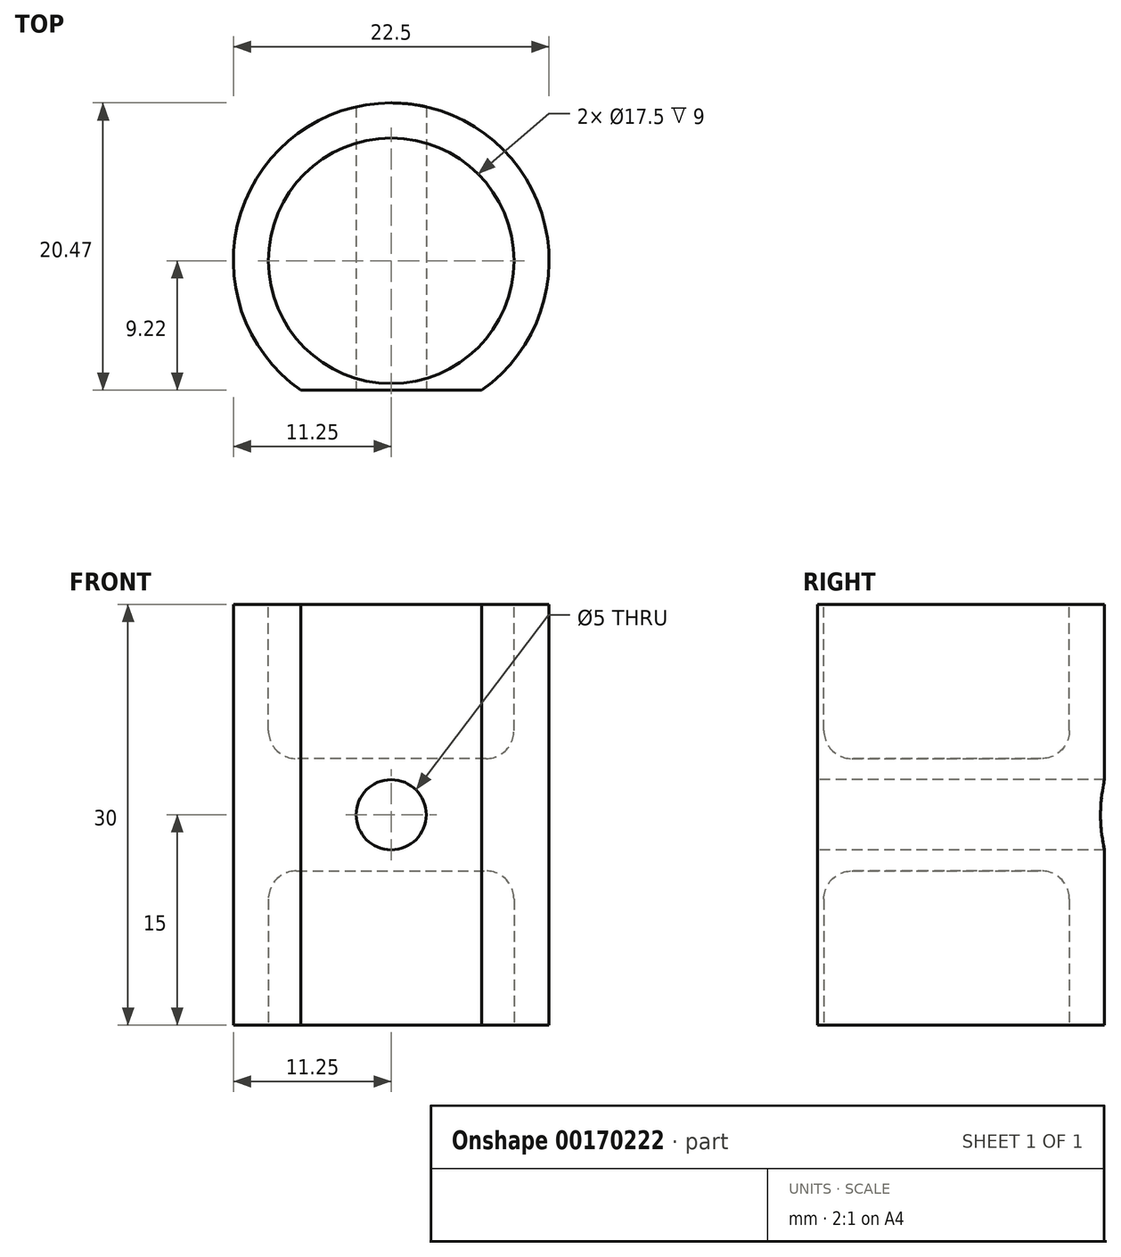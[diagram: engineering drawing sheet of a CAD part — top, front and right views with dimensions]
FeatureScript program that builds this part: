
annotation { "Feature Type Name" : "Feature", "Feature Type Description" : "" }
export const myFeature = defineFeature(function(context is Context, id is Id, definition is map)
    precondition{}
    {
        {
            var Q0;
            Q0=qCreatedBy(makeId("Top.planeOp"),FACE);
            var sketch = newSketch(context, id + "F0", { "sketchPlane" : qUnion([Q0])});
            skCircle(sketch, "E0", {"center": v(0, 0) * mm, "radius": 11.25 * mm});
            skSolve(sketch);
        }
        {
            var Q0;
            Q0=makeQuery(id+"F0.imprint","IMPRINT",FACE,{"disambiguationData":[TD([[makeQuery(id+"F0.imprint","IMPRINT",EDGE,{"derivedFrom":sQuery(id+"F0.wireOp",EDGE,"E0")}),1.0]])]});
            extrude(context, id + "F1", {"entities" : qUnion([Q0]), "depth" : 15 * mm, "hasSecondDirection" : true, "secondDirectionOppositeDirection" : true, "secondDirectionDepth" : 15 * mm});
        }
        {
            var Q0;
            Q0=makeQuery(id+"F1.opExtrude","CAP_FACE",FACE,{"disambiguationData":[OSD([sQuery(id+"F0.wireOp",EDGE,"E0")])],"isStart":false});
            var sketch = newSketch(context, id + "F2", { "sketchPlane" : qUnion([Q0])});
            skCircle(sketch, "E1", {"center": v(0, 0) * mm, "radius": 8.75 * mm});
            skLineSegment(sketch, "E2", {"start": v(-6.45, -9.22) * mm, "end": v(6.45, -9.22) * mm});
            skLineSegment(sketch, "E3", {"start": v(-6.45, -9.22) * mm, "end": v(0, 0) * mm, "construction": true});
            skLineSegment(sketch, "E4", {"start": v(0, 0) * mm, "end": v(6.45, -9.22) * mm, "construction": true});
            skSolve(sketch);
        }
        {
            var Q0;
            Q0=makeQuery(id+"F1.opExtrude","CAP_FACE",FACE,{"disambiguationData":[OSD([sQuery(id+"F0.wireOp",EDGE,"E0")])],"isStart":true});
            var sketch = newSketch(context, id + "F3", { "sketchPlane" : qUnion([Q0])});
            skCircle(sketch, "E5", {"center": v(0, 0) * mm, "radius": 8.75 * mm});
            skSolve(sketch);
        }
        {
            var Q0;
            {var subQ0=sQuery(id+"F2.wireOp",EDGE,"E2");Q0=makeQuery(id+"F2.imprint","IMPRINT",FACE,{"disambiguationData":[TD([[makeQuery(id+"F2.imprint","IMPRINT",EDGE,{"derivedFrom":subQ0}),-1.0]])]});}
            extrude(context, id + "F4", {"entities" : qUnion([Q0]), "operationType" : NewBodyOperationType.REMOVE, "endBound" : BoundingType.THROUGH_ALL, "oppositeDirection" : true, "depth" : 25 * mm});
        }
        {
            var Q0;
            Q0 = qSketchRegion(id + "F2", true);
            extrude(context, id + "F5", {"entities" : qUnion([Q0]), "operationType" : NewBodyOperationType.REMOVE, "oppositeDirection" : true, "depth" : 11 * mm});
        }
        {
            var Q0;
            Q0=makeQuery(id+"F3.imprint","IMPRINT",FACE,{"disambiguationData":[TD([[makeQuery(id+"F3.imprint","IMPRINT",EDGE,{"derivedFrom":sQuery(id+"F3.wireOp",EDGE,"E5")}),1.0]])]});
            var Q1;
            Q1=sQuery(id+"F3.wireOp",EDGE,"E5");
            extrude(context, id + "F6", {"entities" : qUnion([Q0]), "operationType" : NewBodyOperationType.REMOVE, "surfaceEntities" : qUnion([Q1]), "oppositeDirection" : true, "depth" : 11 * mm});
        }
        {
            var Q0;
            Q0=makeQuery(id+"F4.boolean.opBoolean","COPY",FACE,{"derivedFrom":makeQuery(id+"F4.opExtrude","SWEPT_FACE",FACE,{"disambiguationData":[OSD([sQuery(id+"F2.wireOp",EDGE,"E2")])]})});
            var sketch = newSketch(context, id + "F7", { "sketchPlane" : qUnion([Q0])});
            skLineSegment(sketch, "E6", {"start": v(0, 0) * mm, "end": v(0, 15) * mm, "construction": true});
            skSolve(sketch);
        }
        {
            var Q0;
            Q0=sQuery(id+"F7.wireOp",VERTEX,"E6.start");
            var Q1;
            Q1=makeQuery(id+"F1.opExtrude","SWEPT_BODY",BODY,{"disambiguationData":[OSD([sQuery(id+"F0.wireOp",EDGE,"E0")])]});
            hole(context, id + "F8", {"style" : HoleStyle.SIMPLE, "endStyle" : HoleEndStyle.THROUGH, "standardTappedOrClearance" : lookupTablePath({ "standard" : "ISO", "engagement" : "75%", "pitch" : "1 mm", "size" : "M6", "type" : "Tapped" }), "standardBlindInLast" : lookupTablePath({ "standard" : "ISO", "engagement" : "75%", "pitch" : "1 mm", "size" : "M6", "type" : "Tapped" }), "holeDiameter" : 5 * mm, "locations" : qUnion([Q0]), "scope" : qUnion([Q1]), "isTappedThrough" : true, "majorDiameter" : 6 * mm, "showTappedDepth" : true});
        }
        {
            var Q0;
            Q0=makeQuery(id+"F5.boolean.opBoolean","COPY",FACE,{"derivedFrom":makeQuery(id+"F5.opExtrude","CAP_FACE",FACE,{"disambiguationData":[OSD([sQuery(id+"F2.wireOp",EDGE,"E1")])],"isStart":false})});
            fillet(context, id + "F9", {"entities" : qUnion([Q0]), "radius" : 2 * mm, "tangentPropagation" : true, "allowEdgeOverflow" : false});
        }
        {
            var Q0;
            Q0=makeQuery(id+"F6.boolean.opBoolean","COPY",EDGE,{"derivedFrom":makeQuery(id+"F6.opExtrude","CAP_EDGE",EDGE,{"disambiguationData":[OSD([sQuery(id+"F3.wireOp",EDGE,"E5")])],"isStart":false})});
            fillet(context, id + "F10", {"entities" : qUnion([Q0]), "radius" : 2 * mm, "tangentPropagation" : true, "allowEdgeOverflow" : false});
        }
    });
